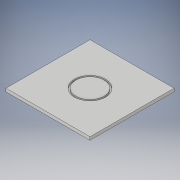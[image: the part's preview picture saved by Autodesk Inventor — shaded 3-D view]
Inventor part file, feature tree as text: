
AUTODESK INVENTOR PART (.ipt)
format: ipt  version: 2019 (Build 230136000, 136)  size: 106,496 bytes
history: native  units: in
note: dims shown in document units (in); Inventor stores cm internally (conversion verified against a paired STEP export)
features: extrude x2, sketch x2
ambient origin geometry x8: Origin, YZ Plane, XZ Plane, XY Plane, X Axis, Y Axis, Z Axis, Center Point
bodies: Solid1 (feature_tree)
feature tree (4):
  extrude  "Extrusion1"  Depth=13.5in
  extrude  "Extrusion2"  Depth=0.25in
  sketch  "Sketch1"  dims[d0=13.5in d1=13.5in]
  sketch  "Sketch2"  dims[d2=0.5in d3=0.0in d4=4.5in d5=0.25in d6=0.25in d7=0.0in]
